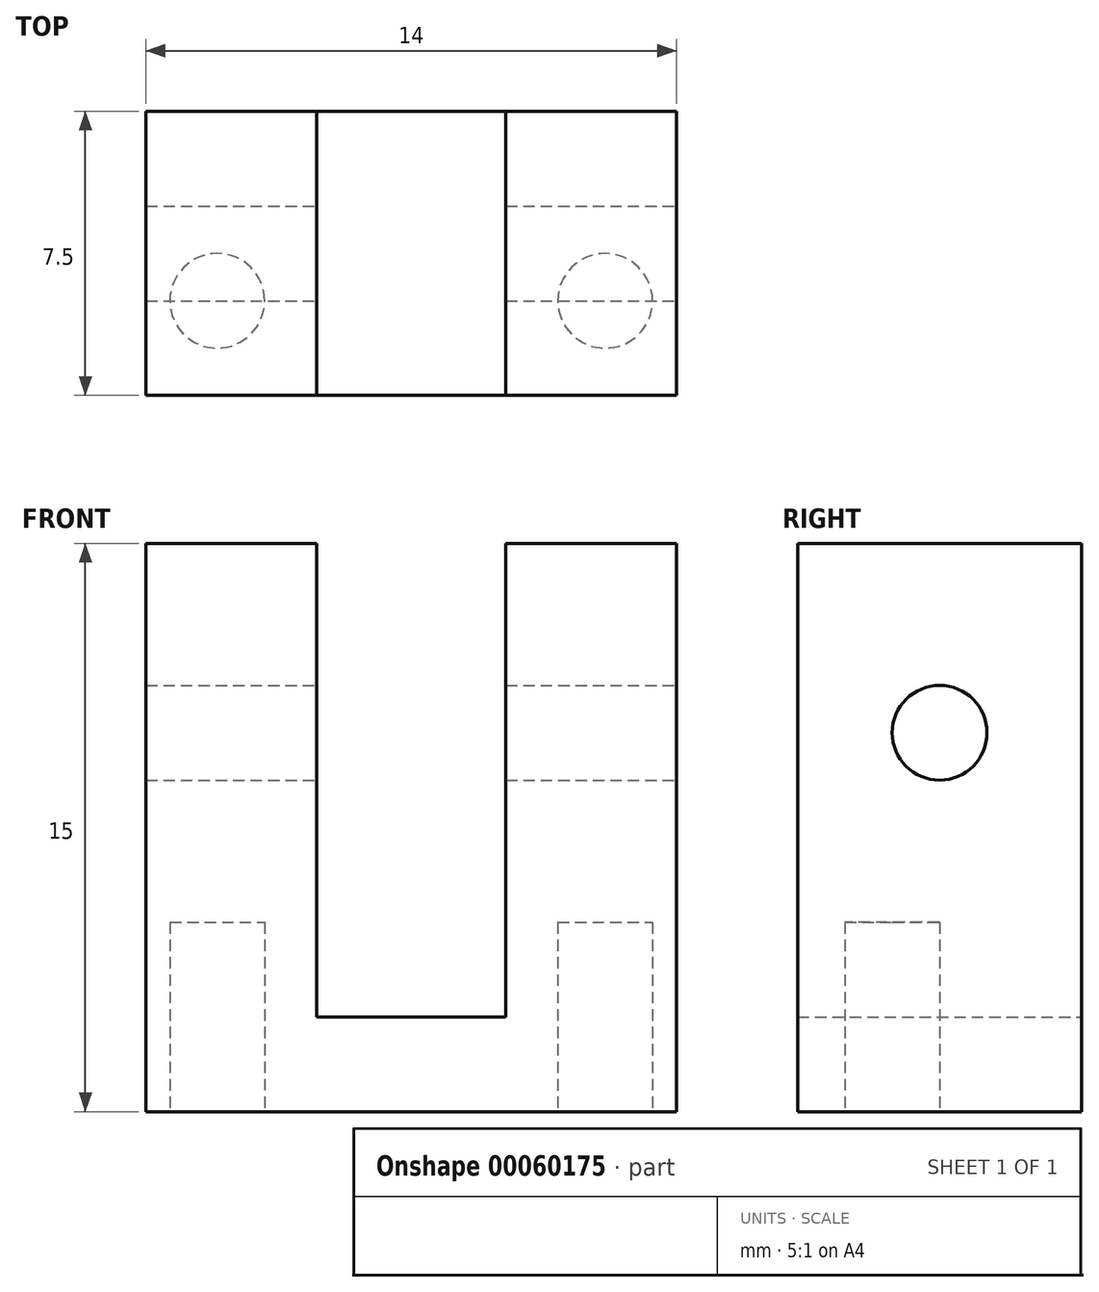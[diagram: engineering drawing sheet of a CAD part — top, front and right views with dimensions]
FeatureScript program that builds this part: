
annotation { "Feature Type Name" : "Feature", "Feature Type Description" : "" }
export const myFeature = defineFeature(function(context is Context, id is Id, definition is map)
    precondition{}
    {
        {
            var Q0;
            Q0=qCreatedBy(makeId("Front.planeOp"),FACE);
            var sketch = newSketch(context, id + "F0", { "sketchPlane" : qUnion([Q0])});
            skLineSegment(sketch, "E0", {"start": v(0, 0) * mm, "end": v(7, 0) * mm});
            skLineSegment(sketch, "E1", {"start": v(7, 0) * mm, "end": v(7, 15) * mm});
            skLineSegment(sketch, "E2", {"start": v(7, 15) * mm, "end": v(2.5, 15) * mm});
            skLineSegment(sketch, "E3", {"start": v(2.5, 15) * mm, "end": v(2.5, 2.5) * mm});
            skLineSegment(sketch, "E4", {"start": v(2.5, 2.5) * mm, "end": v(-2.5, 2.5) * mm});
            skLineSegment(sketch, "E5", {"start": v(-2.5, 2.5) * mm, "end": v(-2.5, 15) * mm});
            skLineSegment(sketch, "E6", {"start": v(-2.5, 15) * mm, "end": v(-7, 15) * mm});
            skLineSegment(sketch, "E7", {"start": v(-7, 15) * mm, "end": v(-7, 0) * mm});
            skLineSegment(sketch, "E8", {"start": v(-7, 0) * mm, "end": v(0, 0) * mm});
            skSolve(sketch);
        }
        {
            var Q0;
            Q0=qSketchRegion(id+"F0",true);
            extrude(context, id + "F1", {"entities" : qUnion([Q0]), "depth" : 7.5 * mm, "symmetric" : true});
        }
        {
            var Q0;
            Q0=makeQuery(id+"F1.opExtrude","SWEPT_FACE",FACE,{"disambiguationData":[OSD([sQuery(id+"F0.wireOp",EDGE,"E1")])]});
            var sketch = newSketch(context, id + "F2", { "sketchPlane" : qUnion([Q0])});
            skCircle(sketch, "E9", {"center": v(0, 10) * mm, "radius": 1.25 * mm});
            skSolve(sketch);
        }
        {
            var Q0;
            Q0=qSketchRegion(id+"F2",true);
            extrude(context, id + "F3", {"entities" : qUnion([Q0]), "operationType" : NewBodyOperationType.REMOVE, "oppositeDirection" : true, "depth" : 25 * mm});
        }
        {
            var Q0;
            Q0=makeQuery(id+"F1.opExtrude","SWEPT_FACE",FACE,{"disambiguationData":[OSD([sQuery(id+"F0.wireOp",EDGE,"E0"),sQuery(id+"F0.wireOp",EDGE,"E8")])]});
            var sketch = newSketch(context, id + "F4", { "sketchPlane" : qUnion([Q0])});
            skCircle(sketch, "E10", {"center": v(5.12, 1.25) * mm, "radius": 1.25 * mm});
            skCircle(sketch, "E11", {"center": v(-5.12, 1.25) * mm, "radius": 1.25 * mm});
            skSolve(sketch);
        }
        {
            var Q0;
            Q0=qSketchRegion(id+"F4",true);
            extrude(context, id + "F5", {"entities" : qUnion([Q0]), "operationType" : NewBodyOperationType.REMOVE, "oppositeDirection" : true, "depth" : 5 * mm});
        }
    });
